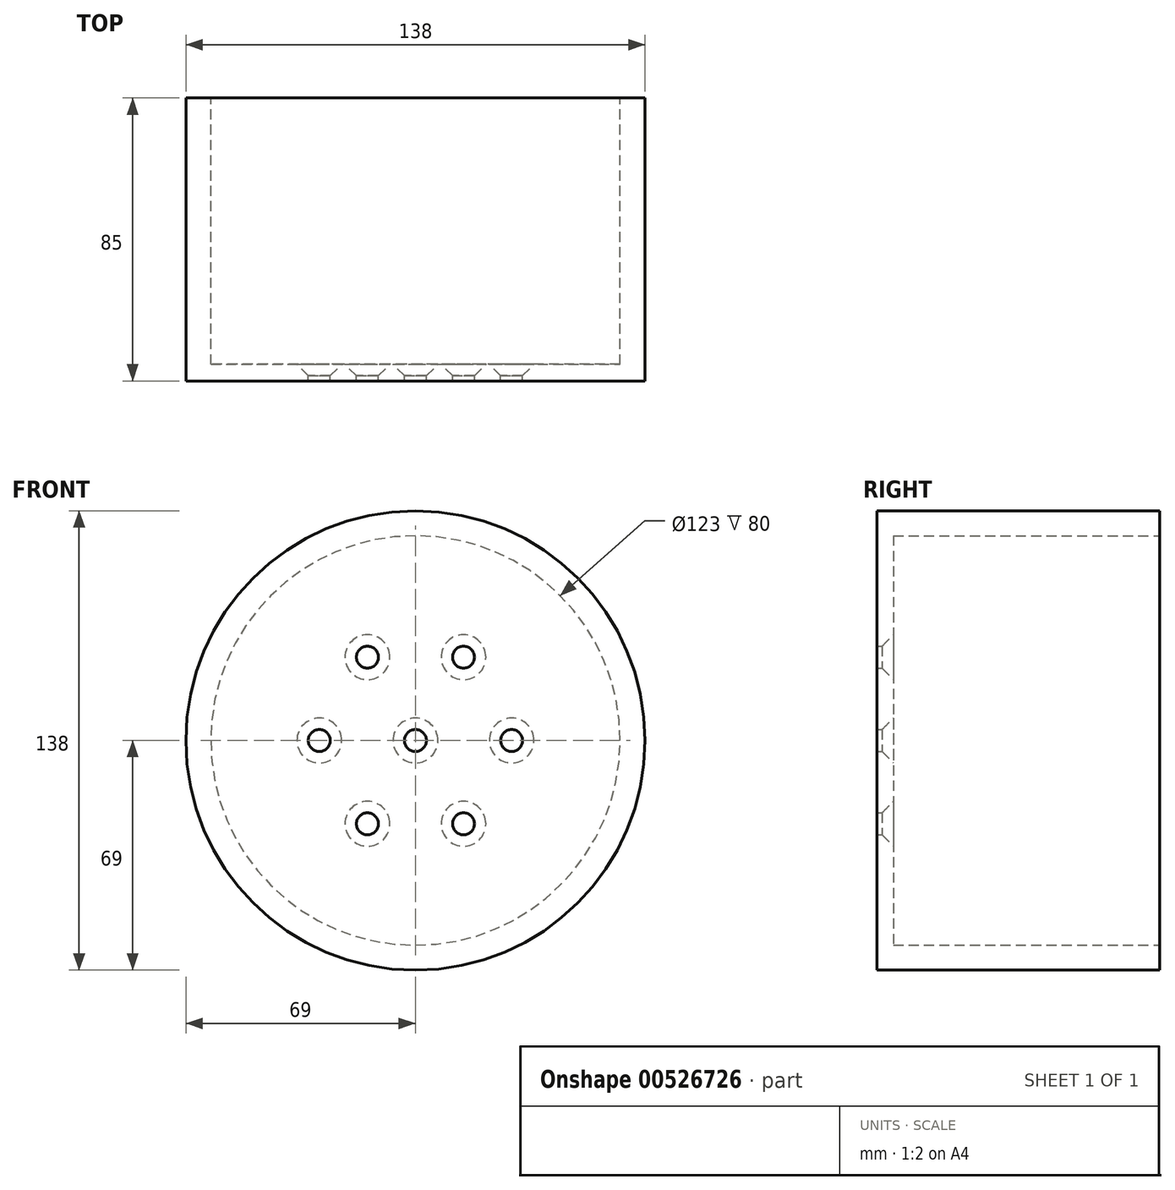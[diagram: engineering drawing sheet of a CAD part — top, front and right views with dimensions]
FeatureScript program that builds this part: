
annotation { "Feature Type Name" : "Feature", "Feature Type Description" : "" }
export const myFeature = defineFeature(function(context is Context, id is Id, definition is map)
    precondition{}
    {
        {
            var Q0;
            Q0=qCreatedBy(makeId("Top.planeOp"),FACE);
            var sketch = newSketch(context, id + "F0", { "sketchPlane" : qUnion([Q0])});
            skPoint(sketch, "E0.middle", {"position": v(0, 0) * mm});
            skLineSegment(sketch, "E1.left", {"start": v(-69, -75) * mm, "end": v(-69, 5) * mm});
            skPoint(sketch, "E1.top.start.orphan", {"position": v(-69, 106.1) * mm});
            skPoint(sketch, "E2.top.start.orphan", {"position": v(-77, 86.5) * mm});
            skPoint(sketch, "E3.orphan", {"position": v(69, 75) * mm});
            skPoint(sketch, "E4.orphan", {"position": v(77, 80) * mm});
            skLineSegment(sketch, "E5", {"start": v(0, 5) * mm, "end": v(0, -83.25) * mm, "construction": true});
            skPoint(sketch, "E6.orphan", {"position": v(69, -106.1) * mm});
            skPoint(sketch, "E7.orphan", {"position": v(77, -86.5) * mm});
            skPoint(sketch, "E0.right.end.orphan", {"position": v(33, 5) * mm});
            skPoint(sketch, "E0.right.start.orphan", {"position": v(33, -5) * mm});
            skLineSegment(sketch, "E8", {"start": v(0, 5) * mm, "end": v(-61.5, 5) * mm});
            skLineSegment(sketch, "E9", {"start": v(-61.5, 5) * mm, "end": v(-61.5, -75) * mm});
            skLineSegment(sketch, "E10", {"start": v(-61.5, -80) * mm, "end": v(-69, -80) * mm});
            skLineSegment(sketch, "E11", {"start": v(-69, -80) * mm, "end": v(-69, -75) * mm});
            skLineSegment(sketch, "E12", {"start": v(-61.5, 5) * mm, "end": v(-69, 5) * mm});
            skLineSegment(sketch, "E13", {"start": v(-69, 5) * mm, "end": v(-69, 5) * mm});
            skLineSegment(sketch, "E14", {"start": v(-61.5, -75) * mm, "end": v(0, -75) * mm});
            skLineSegment(sketch, "E15", {"start": v(0, -75) * mm, "end": v(0, -80) * mm});
            skLineSegment(sketch, "E16", {"start": v(0, -80) * mm, "end": v(-61.5, -80) * mm});
            skSolve(sketch);
        }
        {
            var Q0;
            Q0=qSketchRegion(id+"F0",true);
            var Q1;
            Q1=sQuery(id+"F0.wireOp",EDGE,"E5");
            revolve(context, id + "F1", {"entities" : qUnion([Q0]), "axis" : qUnion([Q1]), "revolveType" : RevolveType.FULL});
        }
        {
            var Q0;
            Q0=makeQuery(id+"F1.opRevolve","SWEPT_FACE",FACE,{"disambiguationData":[OSD([sQuery(id+"F0.wireOp",EDGE,"E14")])]});
            var sketch = newSketch(context, id + "F2", { "sketchPlane" : qUnion([Q0])});
            skCircle(sketch, "E17.cCircle", {"center": v(0, 0) * mm, "radius": 25.03 * mm, "construction": true});
            skLineSegment(sketch, "E17.0", {"start": v(-14.45, -25.03) * mm, "end": v(-28.9, 0) * mm, "construction": true});
            skLineSegment(sketch, "E17.1", {"start": v(-28.9, 0) * mm, "end": v(-14.45, 25.03) * mm, "construction": true});
            skLineSegment(sketch, "E17.2", {"start": v(-14.45, 25.03) * mm, "end": v(14.45, 25.03) * mm, "construction": true});
            skLineSegment(sketch, "E17.3", {"start": v(14.45, 25.03) * mm, "end": v(28.9, 0) * mm, "construction": true});
            skLineSegment(sketch, "E17.4", {"start": v(28.9, 0) * mm, "end": v(14.45, -25.03) * mm, "construction": true});
            skLineSegment(sketch, "E17.5", {"start": v(14.45, -25.03) * mm, "end": v(-14.45, -25.03) * mm, "construction": true});
            skPoint(sketch, "E17.0.midPoint", {"position": v(-21.67, -12.51) * mm});
            skSolve(sketch);
        }
        {
            var Q0;
            Q0=sQuery(id+"F2.wireOp",VERTEX,"E17.3.start");
            var Q1;
            Q1=sQuery(id+"F2.wireOp",VERTEX,"E17.cCircle.center");
            var Q2;
            Q2=sQuery(id+"F2.wireOp",VERTEX,"E17.4.start");
            var Q3;
            Q3=sQuery(id+"F2.wireOp",VERTEX,"E17.5.start");
            var Q4;
            Q4=sQuery(id+"F2.wireOp",VERTEX,"E17.0.start");
            var Q5;
            Q5=sQuery(id+"F2.wireOp",VERTEX,"E17.1.start");
            var Q6;
            Q6=sQuery(id+"F2.wireOp",VERTEX,"E17.2.start");
            var Q7;
            Q7=makeQuery(id+"F1.opRevolve","SWEPT_BODY",BODY,{"disambiguationData":[OSD([sQuery(id+"F0.wireOp",EDGE,"E1.left"),sQuery(id+"F0.wireOp",EDGE,"E9"),sQuery(id+"F0.wireOp",EDGE,"E10"),sQuery(id+"F0.wireOp",EDGE,"E11"),sQuery(id+"F0.wireOp",EDGE,"E12"),sQuery(id+"F0.wireOp",EDGE,"E14"),sQuery(id+"F0.wireOp",EDGE,"E15"),sQuery(id+"F0.wireOp",EDGE,"E16")])]});
            hole(context, id + "F3", {"style" : HoleStyle.C_SINK, "endStyle" : HoleEndStyle.THROUGH, "standardTappedOrClearance" : lookupTablePath({ "standard" : "ISO", "fit" : "Normal", "size" : "M6", "type" : "Clearance" }), "standardBlindInLast" : lookupTablePath({ "fit" : "Standard", "standard" : "ISO", "size" : "M6", "type" : "Clearance" }), "holeDiameter" : 6.6 * mm, "cSinkDiameter" : 13.44 * mm, "cSinkAngle" : 90 * degree, "isTappedThrough" : true, "tappedDepth" : 12 * mm, "tapClearance" : 3, "locations" : qUnion([Q0, Q1, Q2, Q3, Q4, Q5, Q6]), "scope" : qUnion([Q7])});
        }
    });
